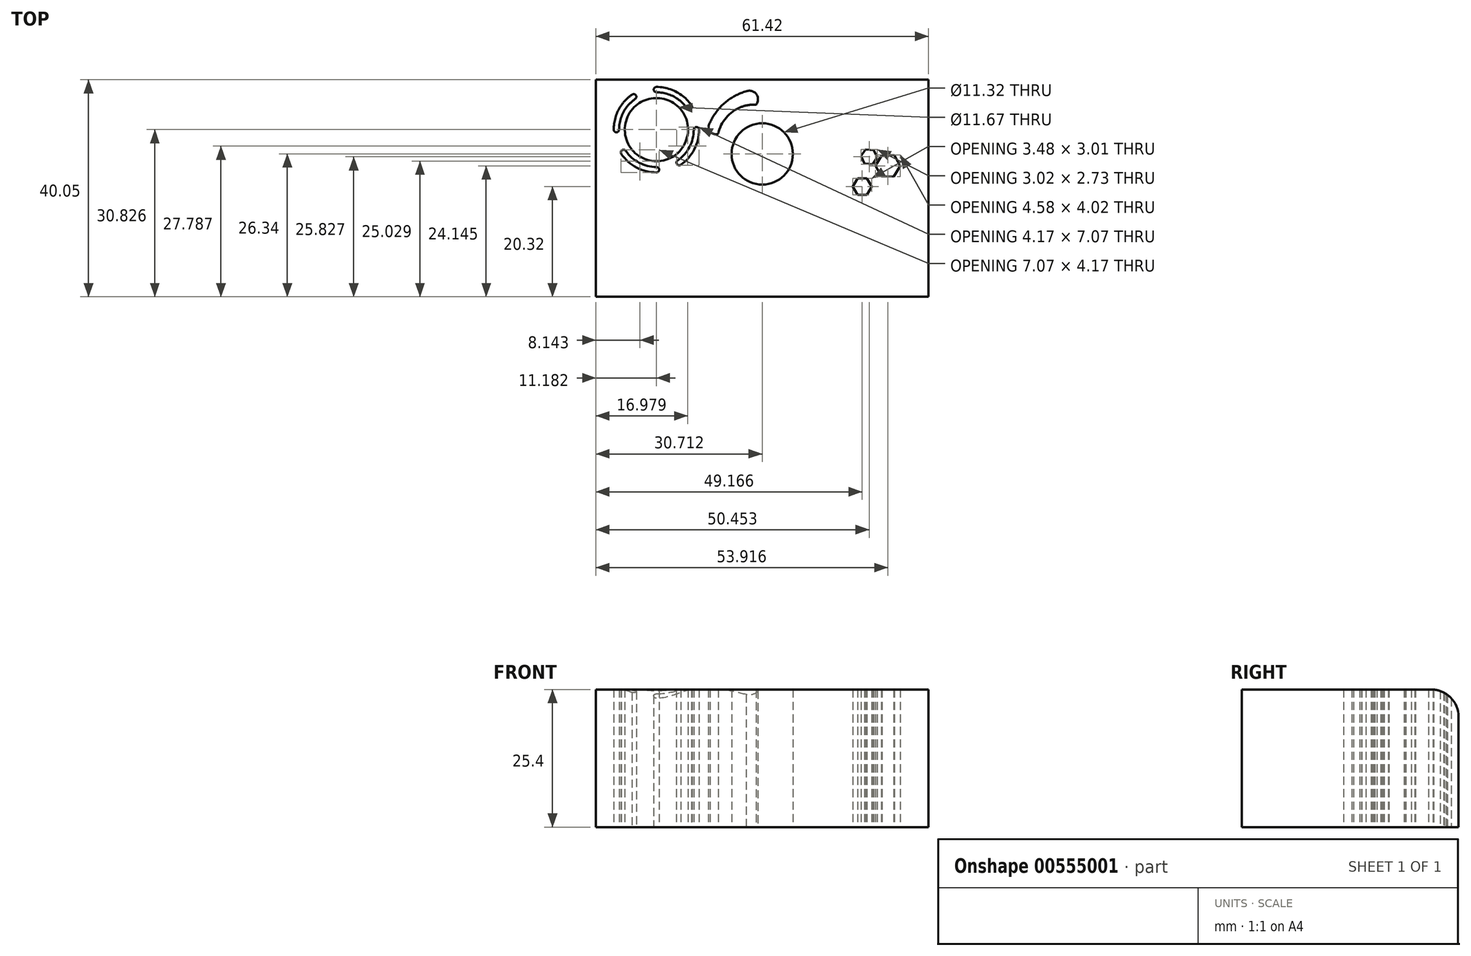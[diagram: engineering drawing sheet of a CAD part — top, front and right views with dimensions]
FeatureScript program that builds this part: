
annotation { "Feature Type Name" : "Feature", "Feature Type Description" : "" }
export const myFeature = defineFeature(function(context is Context, id is Id, definition is map)
    precondition{}
    {
        {
            var Q0;
            Q0=qCreatedBy(makeId("Top.planeOp"),FACE);
            var sketch = newSketch(context, id + "F0", { "sketchPlane" : qUnion([Q0])});
            skLineSegment(sketch, "E0.bottom", {"start": v(-21.07, 19.73) * mm, "end": v(40.35, 19.73) * mm});
            skLineSegment(sketch, "E0.top", {"start": v(-21.07, -20.32) * mm, "end": v(40.35, -20.32) * mm});
            skLineSegment(sketch, "E0.left", {"start": v(-21.07, 19.73) * mm, "end": v(-21.07, -20.32) * mm});
            skLineSegment(sketch, "E0.right", {"start": v(40.35, 19.73) * mm, "end": v(40.35, -20.32) * mm});
            skCircle(sketch, "E1", {"center": v(9.64, 6.02) * mm, "radius": 5.66 * mm});
            skPoint(sketch, "E1.centerSnap0", {"position": v(9.64, 19.73) * mm});
            skArc(sketch, "E2", {"start": v(8.51, 15.11) * mm, "mid": v(4.03, 13.72) * mm, "end": v(1.52, 9.74) * mm});
            skArc(sketch, "E3", {"start": v(6.66, 17.58) * mm, "mid": v(2.69, 15.43) * mm, "end": v(0, 11.8) * mm});
            skArc(sketch, "E4", {"start": v(8.51, 15.11) * mm, "mid": v(8.54, 17.06) * mm, "end": v(6.66, 17.58) * mm});
            skArc(sketch, "E5", {"start": v(0, 11.8) * mm, "mid": v(-0.01, 10.2) * mm, "end": v(1.52, 9.74) * mm});
            skCircle(sketch, "E6", {"center": v(-9.89, 10.5) * mm, "radius": 5.84 * mm});
            skArc(sketch, "E7", {"start": v(-9.89, 18.4) * mm, "mid": v(-6.25, 17.5) * mm, "end": v(-3.43, 15.03) * mm});
            skArc(sketch, "E8", {"start": v(-9.89, 17.4) * mm, "mid": v(-6.69, 16.61) * mm, "end": v(-4.22, 14.42) * mm});
            skArc(sketch, "E9", {"start": v(-4.22, 14.42) * mm, "mid": v(-3.5, 14.31) * mm, "end": v(-3.43, 15.03) * mm});
            skArc(sketch, "E10", {"start": v(-9.89, 17.4) * mm, "mid": v(-10.38, 17.9) * mm, "end": v(-9.89, 18.4) * mm});
            skArc(sketch, "E11.1.0", {"start": v(-16.78, 10.5) * mm, "mid": v(-16, 13.7) * mm, "end": v(-13.8, 16.18) * mm});
            skArc(sketch, "E11.1.1", {"start": v(-17.77, 10.5) * mm, "mid": v(-16.88, 14.14) * mm, "end": v(-14.42, 16.96) * mm});
            skArc(sketch, "E11.1.2", {"start": v(-13.8, 16.18) * mm, "mid": v(-13.7, 16.9) * mm, "end": v(-14.42, 16.96) * mm});
            skArc(sketch, "E11.1.3", {"start": v(-16.78, 10.5) * mm, "mid": v(-17.28, 10.01) * mm, "end": v(-17.77, 10.5) * mm});
            skArc(sketch, "E11.2.0", {"start": v(-9.89, 3.61) * mm, "mid": v(-13.09, 4.4) * mm, "end": v(-15.56, 6.59) * mm});
            skArc(sketch, "E11.2.1", {"start": v(-9.89, 2.62) * mm, "mid": v(-13.53, 3.51) * mm, "end": v(-16.34, 5.98) * mm});
            skArc(sketch, "E11.2.2", {"start": v(-15.56, 6.59) * mm, "mid": v(-16.27, 6.7) * mm, "end": v(-16.34, 5.98) * mm});
            skArc(sketch, "E11.2.3", {"start": v(-9.89, 3.61) * mm, "mid": v(-9.4, 3.12) * mm, "end": v(-9.89, 2.62) * mm});
            skArc(sketch, "E12.1.3.0", {"start": v(-3, 10.5) * mm, "mid": v(-3.78, 7.3) * mm, "end": v(-5.97, 4.84) * mm});
            skArc(sketch, "E12.4.3.0", {"start": v(-2, 10.5) * mm, "mid": v(-2.9, 6.87) * mm, "end": v(-5.36, 4.05) * mm});
            skArc(sketch, "E12.8.3.0", {"start": v(-5.97, 4.84) * mm, "mid": v(-6.08, 4.12) * mm, "end": v(-5.36, 4.05) * mm});
            skArc(sketch, "E12.12.3.0", {"start": v(-3, 10.5) * mm, "mid": v(-2.5, 11) * mm, "end": v(-2, 10.5) * mm});
            skCircle(sketch, "E13.cCircle", {"center": v(28.1, 0) * mm, "radius": 1.74 * mm, "construction": true});
            skLineSegment(sketch, "E13.0", {"start": v(29.84, 0) * mm, "end": v(28.97, -1.5) * mm});
            skLineSegment(sketch, "E13.1", {"start": v(28.97, -1.5) * mm, "end": v(27.23, -1.5) * mm});
            skLineSegment(sketch, "E13.2", {"start": v(27.23, -1.5) * mm, "end": v(26.36, 0) * mm});
            skLineSegment(sketch, "E13.3", {"start": v(26.36, 0) * mm, "end": v(27.23, 1.5) * mm});
            skLineSegment(sketch, "E13.4", {"start": v(27.23, 1.5) * mm, "end": v(28.97, 1.5) * mm});
            skLineSegment(sketch, "E13.5", {"start": v(28.97, 1.5) * mm, "end": v(29.84, 0) * mm});
            skCircle(sketch, "E14.cCircle", {"center": v(29.38, 5.5) * mm, "radius": 1.51 * mm, "construction": true});
            skLineSegment(sketch, "E14.0", {"start": v(30.9, 5.39) * mm, "end": v(30.04, 4.14) * mm});
            skLineSegment(sketch, "E14.1", {"start": v(30.04, 4.14) * mm, "end": v(28.53, 4.26) * mm});
            skLineSegment(sketch, "E14.2", {"start": v(28.53, 4.26) * mm, "end": v(27.87, 5.63) * mm});
            skLineSegment(sketch, "E14.3", {"start": v(27.87, 5.63) * mm, "end": v(28.73, 6.87) * mm});
            skLineSegment(sketch, "E14.4", {"start": v(28.73, 6.87) * mm, "end": v(30.24, 6.75) * mm});
            skLineSegment(sketch, "E14.5", {"start": v(30.24, 6.75) * mm, "end": v(30.9, 5.39) * mm});
            skCircle(sketch, "E15.cCircle", {"center": v(32.85, 3.82) * mm, "radius": 2.3 * mm, "construction": true});
            skLineSegment(sketch, "E15.0", {"start": v(31.66, 1.87) * mm, "end": v(30.56, 3.88) * mm});
            skLineSegment(sketch, "E15.1", {"start": v(30.56, 3.88) * mm, "end": v(31.75, 5.83) * mm});
            skLineSegment(sketch, "E15.2", {"start": v(31.75, 5.83) * mm, "end": v(34.04, 5.78) * mm});
            skLineSegment(sketch, "E15.3", {"start": v(34.04, 5.78) * mm, "end": v(35.14, 3.77) * mm});
            skLineSegment(sketch, "E15.4", {"start": v(35.14, 3.77) * mm, "end": v(33.95, 1.82) * mm});
            skLineSegment(sketch, "E15.5", {"start": v(33.95, 1.82) * mm, "end": v(31.66, 1.87) * mm});
            skSolve(sketch);
        }
        {
            var Q0;
            Q0=makeQuery(id+"F0.imprint","IMPRINT",FACE,{"disambiguationData":[TD([[makeQuery(id+"F0.imprint","IMPRINT",EDGE,{"derivedFrom":sQuery(id+"F0.wireOp",EDGE,"E0.bottom")}),-1.0]])]});
            extrude(context, id + "F1", {"entities" : qUnion([Q0]), "depth" : 25.4 * mm, "offsetDistance" : 25.4 * mm});
        }
        {
            var Q0;
            Q0=makeQuery(id+"F1.opExtrude","CAP_EDGE",EDGE,{"disambiguationData":[OSD([sQuery(id+"F0.wireOp",EDGE,"E0.bottom")])],"isStart":false});
            fillet(context, id + "F2", {"entities" : qUnion([Q0]), "tangentPropagation" : true, "radius" : 5.08 * mm, "defaultsChanged" : false, "vertexSettings" : [], "allowEdgeOverflow" : false});
        }
    });
